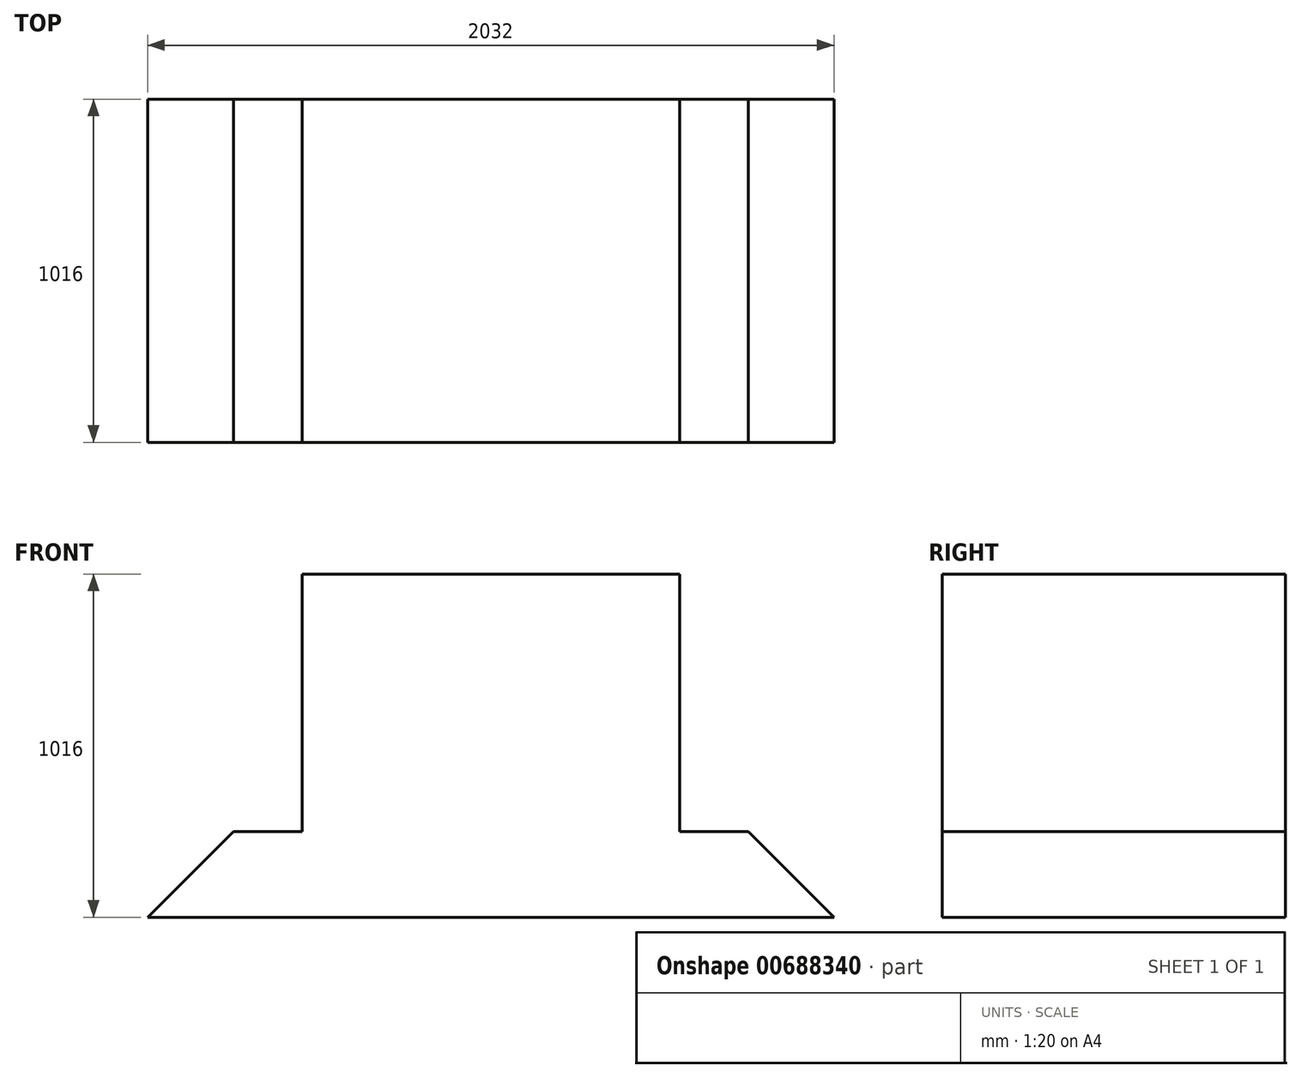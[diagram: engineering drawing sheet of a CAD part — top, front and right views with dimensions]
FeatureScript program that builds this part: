
annotation { "Feature Type Name" : "Feature", "Feature Type Description" : "" }
export const myFeature = defineFeature(function(context is Context, id is Id, definition is map)
    precondition{}
    {
        {
            var Q0;
            Q0=qCreatedBy(makeId("Front.planeOp"),FACE);
            var sketch = newSketch(context, id + "F0", { "sketchPlane" : qUnion([Q0])});
            skLineSegment(sketch, "E0", {"start": v(-988.6, 0) * mm, "end": v(1043.4, 0) * mm});
            skLineSegment(sketch, "E1", {"start": v(1043.4, 0) * mm, "end": v(789.4, 254) * mm});
            skLineSegment(sketch, "E2", {"start": v(789.4, 254) * mm, "end": v(586.2, 254) * mm});
            skLineSegment(sketch, "E3", {"start": v(586.2, 254) * mm, "end": v(586.2, 1016) * mm});
            skLineSegment(sketch, "E4", {"start": v(586.2, 1016) * mm, "end": v(-531.4, 1016) * mm});
            skLineSegment(sketch, "E5", {"start": v(-531.4, 1016) * mm, "end": v(-531.4, 254) * mm});
            skLineSegment(sketch, "E6", {"start": v(-531.4, 254) * mm, "end": v(-734.6, 254) * mm});
            skLineSegment(sketch, "E7", {"start": v(-734.6, 254) * mm, "end": v(-988.6, 0) * mm});
            skSolve(sketch);
        }
        {
            var Q0;
            Q0=makeQuery(id+"F0.imprint","IMPRINT",FACE,{"disambiguationData":[TD([[makeQuery(id+"F0.imprint","IMPRINT",EDGE,{"derivedFrom":sQuery(id+"F0.wireOp",EDGE,"E0")}),1.0]])]});
            extrude(context, id + "F1", {"entities" : qUnion([Q0]), "depth" : 1016 * mm, "offsetDistance" : 25.4 * mm});
        }
    });
